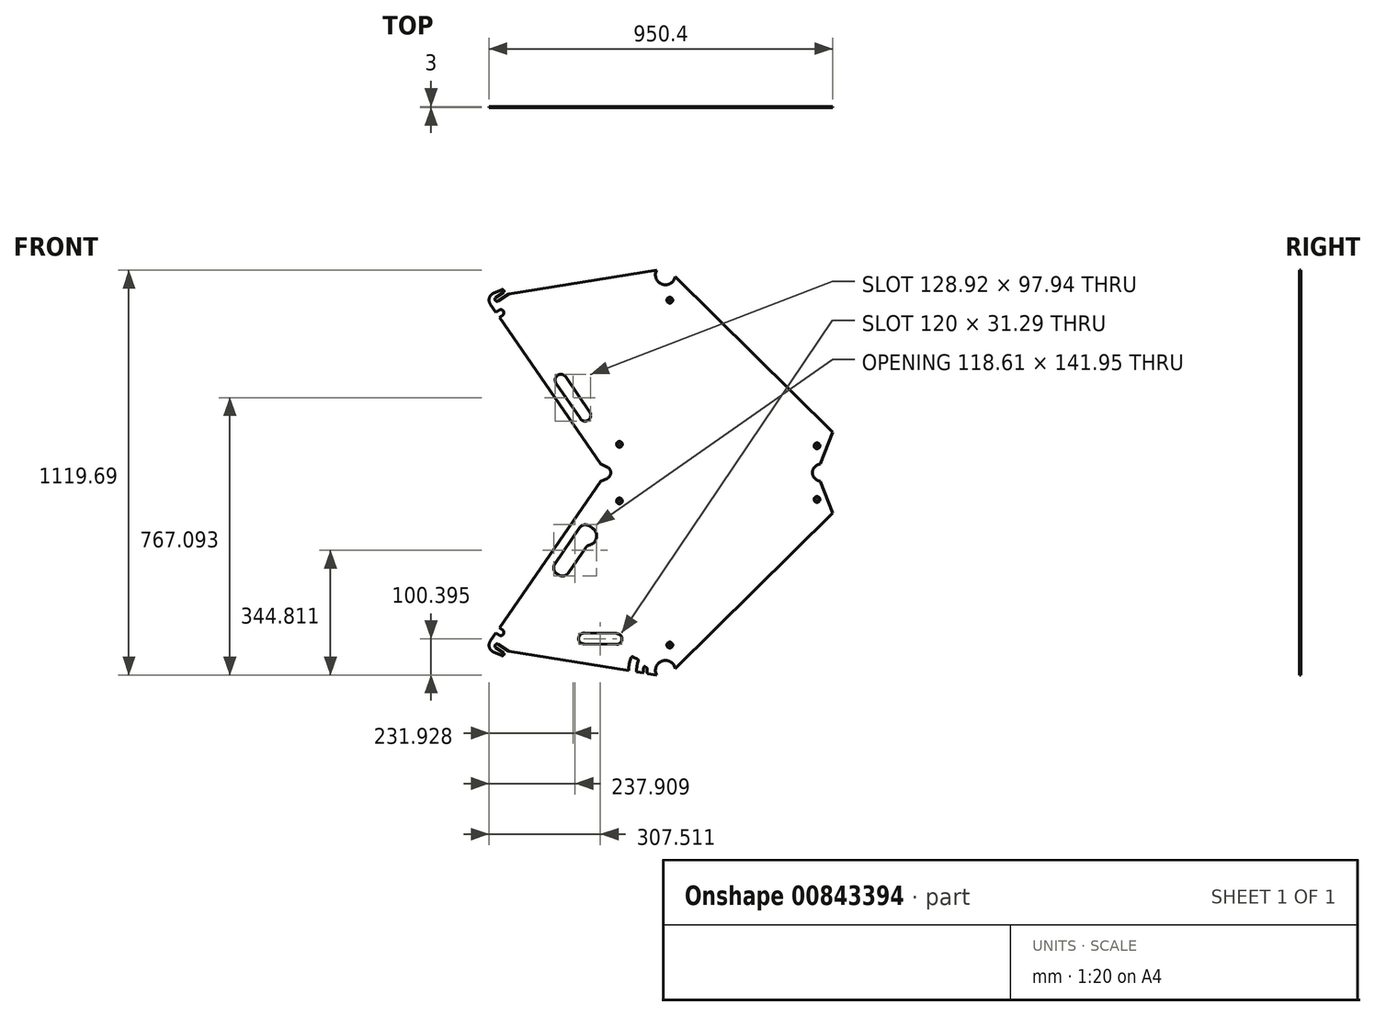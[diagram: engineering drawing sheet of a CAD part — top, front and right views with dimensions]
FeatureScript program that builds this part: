
annotation { "Feature Type Name" : "Feature", "Feature Type Description" : "" }
export const myFeature = defineFeature(function(context is Context, id is Id, definition is map)
    precondition{}
    {
        {
            var Q0;
            Q0=qCreatedBy(makeId("Front.planeOp"),FACE);
            var sketch = newSketch(context, id + "F0", { "sketchPlane" : qUnion([Q0])});
            skCircle(sketch, "E0", {"center": v(1053.9, -134.2) * mm, "radius": 17 * mm, "construction": true});
            skCircle(sketch, "E1", {"center": v(1053.9, -134.2) * mm, "radius": 21.5 * mm, "construction": true});
            skLineSegment(sketch, "E2", {"start": v(622.48, -20.32) * mm, "end": v(871.92, 345.36) * mm, "construction": true});
            skLineSegment(sketch, "E3", {"start": v(615.02, -14.4) * mm, "end": v(879.24, 372.95) * mm, "construction": true});
            skLineSegment(sketch, "E4", {"start": v(1053.9, -134.22) * mm, "end": v(865.03, 414.2) * mm, "construction": true});
            skLineSegment(sketch, "E5", {"start": v(1034.15, -125.7) * mm, "end": v(850, 409.01) * mm, "construction": true});
            skLineSegment(sketch, "E6", {"start": v(861.66, 381.3) * mm, "end": v(851.9, 409.67) * mm, "construction": true});
            skLineSegment(sketch, "E7", {"start": v(1064.21, -115.34) * mm, "end": v(880.07, 419.37) * mm, "construction": true});
            skLineSegment(sketch, "E8", {"start": v(1053.9, -134.2) * mm, "end": v(645.8, -73.78) * mm, "construction": true});
            skLineSegment(sketch, "E9", {"start": v(743.09, -99.4) * mm, "end": v(644.17, -84.76) * mm, "construction": true});
            skLineSegment(sketch, "E10", {"start": v(746.34, -77.44) * mm, "end": v(647.42, -62.8) * mm, "construction": true});
            skLineSegment(sketch, "E11", {"start": v(1035.36, -145.1) * mm, "end": v(841.66, -116.43) * mm, "construction": true});
            skLineSegment(sketch, "E12", {"start": v(1039.32, -118.4) * mm, "end": v(845.61, -89.72) * mm, "construction": true});
            skLineSegment(sketch, "E13", {"start": v(966.15, -134.86) * mm, "end": v(995.58, -139.21) * mm, "construction": true});
            skLineSegment(sketch, "E14", {"start": v(960.23, -139.03) * mm, "end": v(994.85, -144.16) * mm, "construction": true});
            skLineSegment(sketch, "E15", {"start": v(963.6, -143.58) * mm, "end": v(964.04, -140.6) * mm, "construction": true});
            skArc(sketch, "E16", {"start": v(959.64, -143) * mm, "mid": v(959.83, -143.73) * mm, "end": v(960.48, -144.13) * mm, "construction": true});
            skLineSegment(sketch, "E17", {"start": v(960.48, -144.13) * mm, "end": v(962.46, -144.42) * mm, "construction": true});
            skArc(sketch, "E18", {"start": v(962.46, -144.42) * mm, "mid": v(963.2, -144.23) * mm, "end": v(963.6, -143.58) * mm, "construction": true});
            skLineSegment(sketch, "E19", {"start": v(965.3, -133.72) * mm, "end": v(967.21, -120.86) * mm, "construction": true});
            skLineSegment(sketch, "E20", {"start": v(963, -120.24) * mm, "end": v(959.64, -143) * mm, "construction": true});
            skLineSegment(sketch, "E21", {"start": v(962.42, -124.2) * mm, "end": v(966.63, -124.82) * mm, "construction": true});
            skArc(sketch, "E22", {"start": v(965.17, -139.77) * mm, "mid": v(964.43, -139.95) * mm, "end": v(964.04, -140.6) * mm, "construction": true});
            skLineSegment(sketch, "E23", {"start": v(961.7, -129.14) * mm, "end": v(965.9, -129.76) * mm, "construction": true});
            skLineSegment(sketch, "E24", {"start": v(960.08, -126.38) * mm, "end": v(968.24, -127.58) * mm, "construction": true});
            skLineSegment(sketch, "E25", {"start": v(974.82, -141.2) * mm, "end": v(975.55, -136.25) * mm, "construction": true});
            skArc(sketch, "E26", {"start": v(965.3, -133.72) * mm, "mid": v(965.5, -134.46) * mm, "end": v(966.15, -134.86) * mm, "construction": true});
            skLineSegment(sketch, "E27", {"start": v(964.14, -119.4) * mm, "end": v(966.37, -119.73) * mm, "construction": true});
            skArc(sketch, "E28", {"start": v(964.14, -119.4) * mm, "mid": v(963.4, -119.58) * mm, "end": v(963, -120.24) * mm, "construction": true});
            skArc(sketch, "E29", {"start": v(967.21, -120.86) * mm, "mid": v(967.03, -120.12) * mm, "end": v(966.37, -119.73) * mm, "construction": true});
            skLineSegment(sketch, "E30", {"start": v(995.58, -139.21) * mm, "end": v(999.8, -144.9) * mm, "construction": true});
            skLineSegment(sketch, "E31", {"start": v(979.72, -143.94) * mm, "end": v(981.04, -135.04) * mm, "construction": true});
            skArc(sketch, "E32", {"start": v(995.7, -145.3) * mm, "mid": v(995.5, -144.55) * mm, "end": v(994.85, -144.16) * mm, "construction": true});
            skArc(sketch, "E33", {"start": v(995.25, -148.26) * mm, "mid": v(995.44, -149) * mm, "end": v(996.1, -149.4) * mm, "construction": true});
            skArc(sketch, "E34", {"start": v(998.07, -149.7) * mm, "mid": v(998.82, -149.5) * mm, "end": v(999.2, -148.85) * mm, "construction": true});
            skLineSegment(sketch, "E35", {"start": v(996.1, -149.4) * mm, "end": v(998.07, -149.7) * mm, "construction": true});
            skLineSegment(sketch, "E36", {"start": v(999.2, -148.85) * mm, "end": v(999.8, -144.9) * mm, "construction": true});
            skLineSegment(sketch, "E37", {"start": v(995.25, -148.26) * mm, "end": v(995.7, -145.3) * mm, "construction": true});
            skLineSegment(sketch, "E38", {"start": v(985.2, -142.73) * mm, "end": v(985.94, -137.79) * mm, "construction": true});
            skLineSegment(sketch, "E39", {"start": v(995.47, -146.78) * mm, "end": v(993.6, -159.38) * mm, "construction": true});
            skLineSegment(sketch, "E40", {"start": v(850, 409.01) * mm, "end": v(880.07, 419.37) * mm, "construction": true});
            skLineSegment(sketch, "E41", {"start": v(859.77, 380.65) * mm, "end": v(861.66, 381.3) * mm, "construction": true});
            skLineSegment(sketch, "E42", {"start": v(1053.9, -134.22) * mm, "end": v(1520.05, 326.73) * mm, "construction": true});
            skLineSegment(sketch, "E43", {"start": v(1081.03, -129.75) * mm, "end": v(1510.36, 294.78) * mm, "construction": true});
            skLineSegment(sketch, "E44", {"start": v(1060.7, -105.14) * mm, "end": v(1497.91, 327.2) * mm, "construction": true});
            skLineSegment(sketch, "E45", {"start": v(879.24, 372.95) * mm, "end": v(1402.67, 372.95) * mm, "construction": true});
            skLineSegment(sketch, "E46", {"start": v(901.53, 357.05) * mm, "end": v(1486.45, 357.05) * mm, "construction": true});
            skLineSegment(sketch, "E47", {"start": v(890.58, 388.85) * mm, "end": v(1474.25, 388.85) * mm, "construction": true});
            skArc(sketch, "E48", {"start": v(1486.5, 356.93) * mm, "mid": v(1487.54, 375.64) * mm, "end": v(1474.25, 388.85) * mm, "construction": true});
            skArc(sketch, "E49", {"start": v(890.58, 388.85) * mm, "mid": v(888.92, 370.5) * mm, "end": v(901.53, 357.05) * mm, "construction": true});
            skArc(sketch, "E50", {"start": v(1510.36, 294.78) * mm, "mid": v(1511.76, 313.92) * mm, "end": v(1497.91, 327.2) * mm, "construction": true});
            skArc(sketch, "E51", {"start": v(919.09, -223.5) * mm, "mid": v(918.34, -223.31) * mm, "end": v(917.6, -223.13) * mm, "construction": true});
            skFitSpline(sketch, "E52", {"points": [v(871.92, 345.36) * mm, v(875.7, 355.52) * mm, v(881.2, 370.3) * mm, v(868.26, 368.37) * mm, v(864.2, 367.77) * mm], "construction": true});
            skArc(sketch, "E53", {"start": v(591.11, -61.72) * mm, "mid": v(584.1, -63.16) * mm, "end": v(585.54, -70.17) * mm, "construction": true});
            skLineSegment(sketch, "E54", {"start": v(585.54, -70.17) * mm, "end": v(605.08, -83.05) * mm, "construction": true});
            skLineSegment(sketch, "E55", {"start": v(601.55, -93.2) * mm, "end": v(579.26, -83.87) * mm});
            skLineSegment(sketch, "E56", {"start": v(584.15, -63.19) * mm, "end": v(613.37, -82.46) * mm, "construction": true});
            skLineSegment(sketch, "E57", {"start": v(607.46, -8.63) * mm, "end": v(607.4, -8.7) * mm, "construction": true});
            skLineSegment(sketch, "E58", {"start": v(644.18, -84.66) * mm, "end": v(644.29, -83.94) * mm, "construction": true});
            skLineSegment(sketch, "E59", {"start": v(591.11, -61.72) * mm, "end": v(620.67, -81.2) * mm});
            skLineSegment(sketch, "E60", {"start": v(644.18, -84.66) * mm, "end": v(622.66, -81.47) * mm, "construction": true});
            skArc(sketch, "E61", {"start": v(644.63, -83.68) * mm, "mid": v(644.4, -83.74) * mm, "end": v(644.29, -83.94) * mm, "construction": true});
            skLineSegment(sketch, "E62", {"start": v(644.18, -84.66) * mm, "end": v(644.19, -84.63) * mm, "construction": true});
            skArc(sketch, "E63", {"start": v(601.55, -93.2) * mm, "mid": v(607.26, -91.17) * mm, "end": v(605.76, -85.3) * mm});
            skArc(sketch, "E64", {"start": v(617.78, -52.64) * mm, "mid": v(628.06, -58.54) * mm, "end": v(639.47, -61.73) * mm, "construction": true});
            skLineSegment(sketch, "E65", {"start": v(670.48, -77.43) * mm, "end": v(577.33, -63.64) * mm, "construction": true});
            skLineSegment(sketch, "E66", {"start": v(647.4, -62.9) * mm, "end": v(639.47, -61.73) * mm, "construction": true});
            skArc(sketch, "E67", {"start": v(647.3, -63.56) * mm, "mid": v(647.36, -63.78) * mm, "end": v(647.56, -63.9) * mm, "construction": true});
            skLineSegment(sketch, "E68", {"start": v(647.3, -63.56) * mm, "end": v(647.4, -62.9) * mm, "construction": true});
            skArc(sketch, "E69", {"start": v(614, -32.51) * mm, "mid": v(611.92, -43.32) * mm, "end": v(617.78, -52.64) * mm, "construction": true});
            skLineSegment(sketch, "E70", {"start": v(614, -32.51) * mm, "end": v(622.56, -20.17) * mm, "construction": true});
            skLineSegment(sketch, "E71", {"start": v(576.98, -64.11) * mm, "end": v(629.71, 4.8) * mm, "construction": true});
            skArc(sketch, "E72", {"start": v(572.75, -54.03) * mm, "mid": v(569.56, -71.65) * mm, "end": v(582.02, -84.5) * mm, "construction": true});
            skLineSegment(sketch, "E73", {"start": v(607.46, -8.63) * mm, "end": v(608.42, -9.36) * mm, "construction": true});
            skArc(sketch, "E74", {"start": v(621.55, -19.02) * mm, "mid": v(621.5, -19.24) * mm, "end": v(621.6, -19.44) * mm, "construction": true});
            skLineSegment(sketch, "E75", {"start": v(621.6, -19.44) * mm, "end": v(622.56, -20.17) * mm, "construction": true});
            skArc(sketch, "E76", {"start": v(608.42, -9.36) * mm, "mid": v(608.64, -9.42) * mm, "end": v(608.84, -9.3) * mm, "construction": true});
            skLineSegment(sketch, "E77", {"start": v(608.42, -9.36) * mm, "end": v(607.46, -8.63) * mm, "construction": true});
            skLineSegment(sketch, "E78", {"start": v(619.71, -24.29) * mm, "end": v(604.42, -12.6) * mm, "construction": true});
            skCircle(sketch, "E79", {"center": v(600.85, -74.2) * mm, "radius": 5 * mm, "construction": true});
            skLineSegment(sketch, "E80", {"start": v(621.6, -19.44) * mm, "end": v(608.42, -9.36) * mm, "construction": true});
            skLineSegment(sketch, "E81", {"start": v(841.66, -116.43) * mm, "end": v(743.09, -99.4) * mm, "construction": true});
            skLineSegment(sketch, "E82", {"start": v(746.34, -77.44) * mm, "end": v(845.61, -89.72) * mm, "construction": true});
            skEllipse(sketch, "E83", {"center": v(843.64, -103.07) * mm, "majorRadius": 13.5 * mm, "minorRadius": 8.5 * mm, "majorAxis": v(-0.15, -0.99), "construction": true});
            skCircle(sketch, "E84", {"center": v(795.03, 249.5) * mm, "radius": 9.5 * mm, "construction": true});
            skLineSegment(sketch, "E85", {"start": v(796.02, 244.3) * mm, "end": v(795.95, 244.64) * mm, "construction": true});
            skLineSegment(sketch, "E86", {"start": v(796.02, 244.3) * mm, "end": v(789.82, 248.52) * mm, "construction": true});
            skLineSegment(sketch, "E87", {"start": v(784, 242.2) * mm, "end": v(792.26, 236.56) * mm, "construction": true});
            skLineSegment(sketch, "E88", {"start": v(792.26, 236.56) * mm, "end": v(793.8, 238.84) * mm, "construction": true});
            skLineSegment(sketch, "E89", {"start": v(791.91, 236.5) * mm, "end": v(792.26, 236.56) * mm, "construction": true});
            skLineSegment(sketch, "E90", {"start": v(795.95, 244.64) * mm, "end": v(790.17, 248.58) * mm, "construction": true});
            skLineSegment(sketch, "E91", {"start": v(791.91, 236.5) * mm, "end": v(784.06, 241.85) * mm, "construction": true});
            skLineSegment(sketch, "E92", {"start": v(789.96, 238.43) * mm, "end": v(794.75, 245.46) * mm, "construction": true});
            skLineSegment(sketch, "E93", {"start": v(790.2, 238) * mm, "end": v(795.12, 245.2) * mm, "construction": true});
            skLineSegment(sketch, "E94", {"start": v(793.8, 238.84) * mm, "end": v(785.55, 244.47) * mm, "construction": true});
            skLineSegment(sketch, "E95", {"start": v(792.78, 239.54) * mm, "end": v(796.02, 244.3) * mm, "construction": true});
            skArc(sketch, "E96", {"start": v(962.06, -126.67) * mm, "mid": v(930.44, 82.62) * mm, "end": v(787.99, 239.18) * mm, "construction": true});
            skLineSegment(sketch, "E97", {"start": v(702.12, -93.34) * mm, "end": v(670.46, -88.65) * mm, "construction": true});
            skCircle(sketch, "E98", {"center": v(1053.9, -134.2) * mm, "radius": 94.9 * mm, "construction": true});
            skCircle(sketch, "E99", {"center": v(600.85, -74.2) * mm, "radius": 41.4 * mm, "construction": true});
            skLineSegment(sketch, "E100", {"start": v(1055.81, -39.3) * mm, "end": v(601.44, -32.8) * mm, "construction": true});
            skLineSegment(sketch, "E101", {"start": v(1469.36, 401.56) * mm, "end": v(1507.64, 416.26) * mm, "construction": true});
            skLineSegment(sketch, "E102", {"start": v(1507.64, 416.26) * mm, "end": v(1552.44, 299.56) * mm, "construction": true});
            skLineSegment(sketch, "E103", {"start": v(1552.44, 299.56) * mm, "end": v(1514.16, 284.87) * mm, "construction": true});
            skLineSegment(sketch, "E104", {"start": v(1514.16, 284.87) * mm, "end": v(1469.36, 401.56) * mm, "construction": true});
            skLineSegment(sketch, "E105", {"start": v(1516.78, 301.13) * mm, "end": v(1081.03, -129.75) * mm});
            skLineSegment(sketch, "E106", {"start": v(572.75, -54.03) * mm, "end": v(878.77, 388.85) * mm, "construction": true});
            skArc(sketch, "E107", {"start": v(1081.03, -129.75) * mm, "mid": v(1045.11, -108.17) * mm, "end": v(1029.6, -147.1) * mm});
            skLineSegment(sketch, "E108.trimOffspring", {"start": v(1029.6, -147.1) * mm, "end": v(620.67, -81.2) * mm});
            skCircle(sketch, "E109", {"center": v(926.64, 334.5) * mm, "radius": 4 * mm, "construction": true});
            skCircle(sketch, "E110", {"center": v(1472.9, 338.57) * mm, "radius": 4 * mm, "construction": true});
            skCircle(sketch, "E111", {"center": v(1065.9, -64.22) * mm, "radius": 4 * mm, "construction": true});
            skLineSegment(sketch, "E112", {"start": v(1053.9, -134.22) * mm, "end": v(1237.28, -134.22) * mm, "construction": true});
            skLineSegment(sketch, "E113", {"start": v(1053.9, -134.22) * mm, "end": v(1053.9, 23.55) * mm, "construction": true});
            skCircle(sketch, "E114", {"center": v(866.64, 414.5) * mm, "radius": 25 * mm, "construction": true});
            skCircle(sketch, "E115", {"center": v(1489.1, 401.54) * mm, "radius": 28.6 * mm, "construction": true});
            skLineSegment(sketch, "E116", {"start": v(1516.78, 301.13) * mm, "end": v(1482.36, 388.85) * mm});
            skLineSegment(sketch, "E117.trimOffspring", {"start": v(875.12, 388.85) * mm, "end": v(1482.36, 388.85) * mm});
            skCircle(sketch, "E118", {"center": v(600.85, -74.2) * mm, "radius": 312.5 * mm, "construction": true});
            skLineSegment(sketch, "E119.0", {"start": v(570.1, -52.58) * mm, "end": v(585.43, -30.4) * mm});
            skArc(sketch, "E120", {"start": v(570.1, -52.58) * mm, "mid": v(567.23, -70.4) * mm, "end": v(579.26, -83.87) * mm});
            skLineSegment(sketch, "E121.trimOffspring", {"start": v(598.5, -11.47) * mm, "end": v(875.12, 388.85) * mm});
            skArc(sketch, "E122", {"start": v(594.2, -36.46) * mm, "mid": v(610.2, -33.54) * mm, "end": v(607.28, -17.54) * mm, "construction": true});
            skLineSegment(sketch, "E123", {"start": v(600.85, -74.2) * mm, "end": v(600.85, 11.26) * mm, "construction": true});
            skLineSegment(sketch, "E124", {"start": v(594.2, -36.46) * mm, "end": v(585.43, -30.4) * mm, "construction": true});
            skLineSegment(sketch, "E125", {"start": v(607.28, -17.54) * mm, "end": v(598.5, -11.47) * mm, "construction": true});
            skLineSegment(sketch, "E126", {"start": v(598.5, -11.47) * mm, "end": v(595.1, -16.4) * mm});
            skLineSegment(sketch, "E127", {"start": v(595.1, -16.4) * mm, "end": v(603.87, -22.47) * mm});
            skArc(sketch, "E128", {"start": v(594.2, -36.46) * mm, "mid": v(606.03, -34.3) * mm, "end": v(603.87, -22.47) * mm});
            skLineSegment(sketch, "E129", {"start": v(585.43, -30.4) * mm, "end": v(594.2, -36.46) * mm});
            skLineSegment(sketch, "E130", {"start": v(584.23, -71.1) * mm, "end": v(605.76, -85.3) * mm});
            skArc(sketch, "E131", {"start": v(591.11, -61.72) * mm, "mid": v(583.83, -63.6) * mm, "end": v(584.23, -71.1) * mm});
            skSolve(sketch);
        }
        {
            var Q0;
            Q0=qSketchRegion(id+"F0",true);
            extrude(context, id + "F1", {"entities" : qUnion([Q0]), "depth" : 3 * mm, "offsetDistance" : 25 * mm});
        }
        {
            var Q0;
            Q0=makeQuery(id+"F1.opExtrude","SWEPT_FACE",FACE,{"disambiguationData":[OSD([sQuery(id+"F0.wireOp",EDGE,"E117.trimOffspring")])]});
            cPlane(context, id + "F2", {"entities" : qUnion([Q0]), "cplaneType" : CPlaneType.OFFSET, "offset" : 23.9 * mm, "width" : 150 * mm, "height" : 150 * mm});
        }
        {
            var Q0;
            Q0=makeQuery(id+"F1.opExtrude","SWEPT_BODY",BODY,{"disambiguationData":[OSD([sQuery(id+"F0.wireOp",EDGE,"E53"),sQuery(id+"F0.wireOp",EDGE,"E54"),sQuery(id+"F0.wireOp",EDGE,"E55"),sQuery(id+"F0.wireOp",EDGE,"E59"),sQuery(id+"F0.wireOp",EDGE,"c0fece56-cd10-4327-9040-2cab23e675d4"),sQuery(id+"F0.wireOp",EDGE,"E63"),sQuery(id+"F0.wireOp",EDGE,"E72"),sQuery(id+"F0.wireOp",EDGE,"PVY0APLz-6rdr-JrDk-CvCb-vWmYWycaJObT"),sQuery(id+"F0.wireOp",EDGE,"rSiPkJzu-22ck-wLmw-T34Z-YrS7vC3DeLN9"),sQuery(id+"F0.wireOp",EDGE,"E105"),sQuery(id+"F0.wireOp",EDGE,"E106"),sQuery(id+"F0.wireOp",EDGE,"E107"),sQuery(id+"F0.wireOp",EDGE,"E108.trimOffspring")])]});
            var Q1;
            Q1=qCreatedBy(id+"F2.planeOp",FACE);
            mirror(context, id + "F3", {"entities" : qUnion([Q0]), "mirrorPlane" : qUnion([Q1])});
        }
        {
            var Q0;
            Q0=makeQuery(id+"F1.opExtrude","CAP_FACE",FACE,{"disambiguationData":[OSD([sQuery(id+"F0.wireOp",EDGE,"E53"),sQuery(id+"F0.wireOp",EDGE,"E54"),sQuery(id+"F0.wireOp",EDGE,"E55"),sQuery(id+"F0.wireOp",EDGE,"E59"),sQuery(id+"F0.wireOp",EDGE,"c0fece56-cd10-4327-9040-2cab23e675d4"),sQuery(id+"F0.wireOp",EDGE,"E63"),sQuery(id+"F0.wireOp",EDGE,"E72"),sQuery(id+"F0.wireOp",EDGE,"PVY0APLz-6rdr-JrDk-CvCb-vWmYWycaJObT"),sQuery(id+"F0.wireOp",EDGE,"rSiPkJzu-22ck-wLmw-T34Z-YrS7vC3DeLN9"),sQuery(id+"F0.wireOp",EDGE,"E105"),sQuery(id+"F0.wireOp",EDGE,"E106"),sQuery(id+"F0.wireOp",EDGE,"E107"),sQuery(id+"F0.wireOp",EDGE,"E108.trimOffspring")])],"isStart":false});
            var sketch = newSketch(context, id + "F4", { "sketchPlane" : qUnion([Q0])});
            skLineSegment(sketch, "E132", {"start": v(885.12, 412.75) * mm, "end": v(1482.36, 412.75) * mm, "construction": true});
            skLineSegment(sketch, "E133.0", {"start": v(1516.78, 524.37) * mm, "end": v(1482.36, 436.65) * mm, "construction": true});
            skLineSegment(sketch, "E134", {"start": v(1482.36, 388.85) * mm, "end": v(1516.78, 301.13) * mm, "construction": true});
            skArc(sketch, "E135", {"start": v(892.46, 396.86) * mm, "mid": v(902.62, 412.75) * mm, "end": v(892.46, 428.63) * mm});
            skArc(sketch, "E136", {"start": v(1474.77, 433.93) * mm, "mid": v(1459.86, 412.75) * mm, "end": v(1474.77, 391.57) * mm});
            skLineSegment(sketch, "E137", {"start": v(875.12, 388.85) * mm, "end": v(1482.36, 388.85) * mm});
            skLineSegment(sketch, "E138", {"start": v(1482.36, 436.65) * mm, "end": v(875.12, 436.65) * mm});
            skLineSegment(sketch, "E139", {"start": v(875.12, 436.65) * mm, "end": v(892.46, 428.63) * mm});
            skLineSegment(sketch, "E140", {"start": v(875.12, 388.85) * mm, "end": v(892.46, 396.86) * mm});
            skLineSegment(sketch, "E141", {"start": v(1482.36, 388.85) * mm, "end": v(1474.77, 391.57) * mm});
            skLineSegment(sketch, "E142", {"start": v(1482.36, 436.65) * mm, "end": v(1474.77, 433.93) * mm});
            skLineSegment(sketch, "E143", {"start": v(1482.36, 436.65) * mm, "end": v(1482.36, 388.85) * mm, "construction": true});
            skSolve(sketch);
        }
        {
            var Q0;
            Q0=qSketchRegion(id+"F4",true);
            var Q1;
            Q1=makeQuery(id+"F3.opPattern","COPY",FACE,{"derivedFrom":makeQuery(id+"F1.opExtrude","CAP_FACE",FACE,{"disambiguationData":[OSD([sQuery(id+"F0.wireOp",EDGE,"E53"),sQuery(id+"F0.wireOp",EDGE,"E54"),sQuery(id+"F0.wireOp",EDGE,"E55"),sQuery(id+"F0.wireOp",EDGE,"E59"),sQuery(id+"F0.wireOp",EDGE,"c0fece56-cd10-4327-9040-2cab23e675d4"),sQuery(id+"F0.wireOp",EDGE,"E63"),sQuery(id+"F0.wireOp",EDGE,"E72"),sQuery(id+"F0.wireOp",EDGE,"PVY0APLz-6rdr-JrDk-CvCb-vWmYWycaJObT"),sQuery(id+"F0.wireOp",EDGE,"rSiPkJzu-22ck-wLmw-T34Z-YrS7vC3DeLN9"),sQuery(id+"F0.wireOp",EDGE,"E105"),sQuery(id+"F0.wireOp",EDGE,"E106"),sQuery(id+"F0.wireOp",EDGE,"E107"),sQuery(id+"F0.wireOp",EDGE,"E108.trimOffspring")])],"isStart":true}),"instanceName":"1"});
            extrude(context, id + "F5", {"entities" : qUnion([Q0]), "operationType" : NewBodyOperationType.ADD, "endBound" : BoundingType.UP_TO_SURFACE, "oppositeDirection" : true, "depth" : 65 * mm, "endBoundEntityFace" : qUnion([Q1]), "offsetDistance" : 25 * mm});
        }
        {
            var Q0;
            {var subQ0=makeQuery(id+"F1.opExtrude","CAP_FACE",FACE,{"disambiguationData":[OSD([sQuery(id+"F0.wireOp",EDGE,"E53"),sQuery(id+"F0.wireOp",EDGE,"E54"),sQuery(id+"F0.wireOp",EDGE,"E55"),sQuery(id+"F0.wireOp",EDGE,"E59"),sQuery(id+"F0.wireOp",EDGE,"E63"),sQuery(id+"F0.wireOp",EDGE,"E72"),sQuery(id+"F0.wireOp",EDGE,"PVY0APLz-6rdr-JrDk-CvCb-vWmYWycaJObT"),sQuery(id+"F0.wireOp",EDGE,"rSiPkJzu-22ck-wLmw-T34Z-YrS7vC3DeLN9"),sQuery(id+"F0.wireOp",EDGE,"E105"),sQuery(id+"F0.wireOp",EDGE,"E106"),sQuery(id+"F0.wireOp",EDGE,"E107"),sQuery(id+"F0.wireOp",EDGE,"E108.trimOffspring"),sQuery(id+"F0.wireOp",EDGE,"E109"),sQuery(id+"F0.wireOp",EDGE,"E110"),sQuery(id+"F0.wireOp",EDGE,"E111")])],"isStart":false});Q0=makeQuery(id+"F5.boolean.opBoolean","MERGE",FACE,{"derivedFrom":[subQ0,makeQuery(id+"F3.opPattern","COPY",FACE,{"derivedFrom":subQ0,"instanceName":"1"}),makeQuery(id+"F5.opExtrude","CAP_FACE",FACE,{"disambiguationData":[OSD([sQuery(id+"F4.wireOp",EDGE,"yLFeXnhX-FHJ1-lWFD-LUYU-IVhkZNTNpous"),sQuery(id+"F4.wireOp",EDGE,"25Roz2r3-I6Ic-58va-7k2N-V37a2FIcnueW"),sQuery(id+"F4.wireOp",EDGE,"Mdtmx1y3-Aq5y-VBCD-G2xE-9g1DUSUnupkp"),sQuery(id+"F4.wireOp",EDGE,"31XSQ7MP-bYWI-LpWw-hrBR-gacfVsKKRKhD")])],"isStart":true})]});}
            var sketch = newSketch(context, id + "F6", { "sketchPlane" : qUnion([Q0])});
            skLineSegment(sketch, "E144.bottom", {"start": v(829.1, -31.06) * mm, "end": v(919.1, -32.35) * mm});
            skLineSegment(sketch, "E144.top", {"start": v(828.68, -61.06) * mm, "end": v(918.68, -62.35) * mm});
            skArc(sketch, "E145", {"start": v(829.1, -31.06) * mm, "mid": v(813.9, -45.85) * mm, "end": v(828.68, -61.06) * mm});
            skArc(sketch, "E146", {"start": v(918.68, -62.35) * mm, "mid": v(933.89, -47.56) * mm, "end": v(919.1, -32.35) * mm});
            skCircle(sketch, "E147", {"center": v(1053.9, -134.22) * mm, "radius": 101.64 * mm, "construction": true});
            skPoint(sketch, "E148.0", {"position": v(1035.36, -145.1) * mm});
            skLineSegment(sketch, "E149.0", {"start": v(1035.36, -145.1) * mm, "end": v(841.66, -116.43) * mm, "construction": true});
            skPoint(sketch, "E150", {"position": v(952.27, -132.8) * mm});
            skCircle(sketch, "E151", {"center": v(1053.9, -134.22) * mm, "radius": 79.64 * mm, "construction": true});
            skPoint(sketch, "E152", {"position": v(1003.7, -140.42) * mm});
            skCircle(sketch, "E153", {"center": v(1053.9, -134.22) * mm, "radius": 50.57 * mm, "construction": true});
            skCircle(sketch, "E154", {"center": v(1053.9, -134.22) * mm, "radius": 60.57 * mm, "construction": true});
            skArc(sketch, "E155", {"start": v(958.14, -100.13) * mm, "mid": v(953.7, -117.13) * mm, "end": v(952.26, -134.64) * mm});
            skArc(sketch, "E156", {"start": v(978.53, -108.48) * mm, "mid": v(975.03, -123.14) * mm, "end": v(974.36, -138.2) * mm});
            skArc(sketch, "E157", {"start": v(964.95, -97.27) * mm, "mid": v(960.92, -97.2) * mm, "end": v(958.14, -100.13) * mm});
            skLineSegment(sketch, "E158", {"start": v(964.95, -97.27) * mm, "end": v(975.9, -102.33) * mm});
            skArc(sketch, "E159", {"start": v(978.53, -108.48) * mm, "mid": v(978.4, -104.9) * mm, "end": v(975.9, -102.33) * mm});
            skLineSegment(sketch, "E160", {"start": v(952.26, -134.64) * mm, "end": v(974.36, -138.2) * mm});
            skArc(sketch, "E161", {"start": v(993.88, -126.05) * mm, "mid": v(993.33, -133.68) * mm, "end": v(993.74, -141.32) * mm});
            skArc(sketch, "E162", {"start": v(1003.55, -129.43) * mm, "mid": v(1003.37, -136.22) * mm, "end": v(1004.1, -142.99) * mm});
            skLineSegment(sketch, "E163", {"start": v(998.61, -124.02) * mm, "end": v(1002.33, -126.71) * mm});
            skPoint(sketch, "E164.visualSharp", {"position": v(994.74, -121.22) * mm});
            skArc(sketch, "E164.filletArc", {"start": v(998.61, -124.02) * mm, "mid": v(995.67, -123.7) * mm, "end": v(993.88, -126.05) * mm});
            skPoint(sketch, "E165.visualSharp", {"position": v(1003.74, -127.74) * mm});
            skArc(sketch, "E165.filletArc", {"start": v(1003.55, -129.43) * mm, "mid": v(1003.3, -127.9) * mm, "end": v(1002.33, -126.71) * mm});
            skLineSegment(sketch, "E166", {"start": v(993.74, -141.32) * mm, "end": v(1004.1, -142.99) * mm});
            skSolve(sketch);
        }
        {
            var Q0;
            Q0=qSketchRegion(id+"F6",true);
            extrude(context, id + "F7", {"entities" : qUnion([Q0]), "operationType" : NewBodyOperationType.REMOVE, "oppositeDirection" : true, "depth" : 25 * mm, "offsetDistance" : 25 * mm});
        }
        {
            var Q0;
            Q0=makeQuery(id+"F4.imprint","IMPRINT",FACE,{"disambiguationData":[TD([[makeQuery(id+"F4.imprint","IMPRINT",EDGE,{"derivedFrom":sQuery(id+"F4.wireOp",EDGE,"E137")}),-1.0]])]});
            var sketch = newSketch(context, id + "F8", { "sketchPlane" : qUnion([Q0])});
            skLineSegment(sketch, "E167", {"start": v(748.46, 160.82) * mm, "end": v(816.08, 259.96) * mm});
            skLineSegment(sketch, "E168", {"start": v(843.88, 265.2) * mm, "end": v(852.14, 259.57) * mm});
            skLineSegment(sketch, "E169", {"start": v(757.84, 130.21) * mm, "end": v(753.71, 133.03) * mm});
            skCircle(sketch, "E170.0", {"center": v(600.85, -74.2) * mm, "radius": 312.5 * mm, "construction": true});
            skLineSegment(sketch, "E170.1", {"start": v(622.48, -20.32) * mm, "end": v(871.92, 345.36) * mm, "construction": true});
            skLineSegment(sketch, "E171.0", {"start": v(885.12, 412.75) * mm, "end": v(1482.36, 412.75) * mm, "construction": true});
            skCircle(sketch, "E172.MirrorC", {"center": v(600.85, 899.7) * mm, "radius": 312.5 * mm, "construction": true});
            skLineSegment(sketch, "E173.MirrorCS", {"start": v(622.48, 845.82) * mm, "end": v(871.92, 480.13) * mm, "construction": true});
            skLineSegment(sketch, "E174", {"start": v(818.34, 562.24) * mm, "end": v(751.84, 659.72) * mm});
            skLineSegment(sketch, "E175", {"start": v(756.04, 681.95) * mm, "end": v(756.04, 681.95) * mm});
            skLineSegment(sketch, "E176", {"start": v(778.28, 677.75) * mm, "end": v(844.77, 580.27) * mm});
            skLineSegment(sketch, "E177", {"start": v(840.57, 558.04) * mm, "end": v(840.57, 558.04) * mm});
            skLineSegment(sketch, "E178.0", {"start": v(797.53, 236.3) * mm, "end": v(785.55, 244.47) * mm, "construction": true});
            skLineSegment(sketch, "E179.MirrorCS", {"start": v(797.53, 589.2) * mm, "end": v(785.55, 581.03) * mm, "construction": true});
            skLineSegment(sketch, "E180", {"start": v(797.53, 589.2) * mm, "end": v(768.19, 569.19) * mm, "construction": true});
            skPoint(sketch, "E181.orphan", {"position": v(793.8, 586.66) * mm});
            skPoint(sketch, "E182.orphan", {"position": v(793.8, 238.84) * mm});
            skLineSegment(sketch, "E183", {"start": v(797.53, 236.3) * mm, "end": v(778.55, 249.24) * mm, "construction": true});
            skPoint(sketch, "E184.visualSharp", {"position": v(827.35, 276.48) * mm});
            skArc(sketch, "E184.filletArc", {"start": v(843.88, 265.2) * mm, "mid": v(828.9, 268.34) * mm, "end": v(816.08, 259.96) * mm});
            skPoint(sketch, "E185.visualSharp", {"position": v(872.79, 245.49) * mm});
            skArc(sketch, "E185.filletArc", {"start": v(842.48, 211.69) * mm, "mid": v(863.19, 232.43) * mm, "end": v(852.14, 259.57) * mm});
            skPoint(sketch, "E186.visualSharp", {"position": v(737.2, 144.3) * mm});
            skArc(sketch, "E186.filletArc", {"start": v(748.46, 160.82) * mm, "mid": v(745.33, 145.84) * mm, "end": v(753.71, 133.03) * mm});
            skPoint(sketch, "E187.visualSharp", {"position": v(782.63, 113.3) * mm});
            skArc(sketch, "E187.filletArc", {"start": v(757.84, 130.21) * mm, "mid": v(772.83, 127.08) * mm, "end": v(785.64, 135.47) * mm});
            skPoint(sketch, "E188.visualSharp", {"position": v(742.83, 672.94) * mm});
            skArc(sketch, "E188.filletArc", {"start": v(756.04, 681.95) * mm, "mid": v(749.34, 671.7) * mm, "end": v(751.84, 659.72) * mm});
            skPoint(sketch, "E189.visualSharp", {"position": v(769.26, 690.97) * mm});
            skArc(sketch, "E189.filletArc", {"start": v(778.28, 677.75) * mm, "mid": v(768.03, 684.46) * mm, "end": v(756.04, 681.95) * mm});
            skPoint(sketch, "E190.visualSharp", {"position": v(853.79, 567.05) * mm});
            skArc(sketch, "E190.filletArc", {"start": v(840.57, 558.04) * mm, "mid": v(847.28, 568.28) * mm, "end": v(844.77, 580.27) * mm});
            skPoint(sketch, "E191.visualSharp", {"position": v(827.35, 549.02) * mm});
            skArc(sketch, "E191.filletArc", {"start": v(818.34, 562.24) * mm, "mid": v(828.58, 555.53) * mm, "end": v(840.57, 558.04) * mm});
            skLineSegment(sketch, "E192", {"start": v(785.64, 135.47) * mm, "end": v(833.6, 205.8) * mm});
            skArc(sketch, "E193", {"start": v(842.48, 211.69) * mm, "mid": v(837.47, 209.6) * mm, "end": v(833.6, 205.8) * mm});
            skSolve(sketch);
        }
        {
            var Q0;
            Q0=qSketchRegion(id+"F8",true);
            extrude(context, id + "F9", {"entities" : qUnion([Q0]), "operationType" : NewBodyOperationType.REMOVE, "endBound" : BoundingType.THROUGH_ALL, "oppositeDirection" : true, "depth" : 25 * mm, "offsetDistance" : 25 * mm});
        }
        {
            var Q0;
            Q0=makeQuery(id+"F4.imprint","IMPRINT",FACE,{"disambiguationData":[TD([[makeQuery(id+"F4.imprint","IMPRINT",EDGE,{"derivedFrom":sQuery(id+"F4.wireOp",EDGE,"E137")}),-1.0]])]});
            var sketch = newSketch(context, id + "F10", { "sketchPlane" : qUnion([Q0])});
            skPoint(sketch, "E194.0", {"position": v(926.64, 334.5) * mm});
            skPoint(sketch, "E194.1", {"position": v(1472.9, 338.57) * mm});
            skPoint(sketch, "E194.2", {"position": v(1065.9, -64.22) * mm});
            skPoint(sketch, "E195.MirrorP", {"position": v(926.64, 491) * mm});
            skPoint(sketch, "E196.MirrorP", {"position": v(1472.9, 486.93) * mm});
            skPoint(sketch, "E197.MirrorP", {"position": v(1065.9, 889.72) * mm});
            skSolve(sketch);
        }
        {
            var Q0;
            Q0=sQuery(id+"F10.wireOp",VERTEX,"E197.MirrorP");
            var Q1;
            Q1=sQuery(id+"F10.wireOp",VERTEX,"E195.MirrorP");
            var Q2;
            Q2=sQuery(id+"F10.wireOp",VERTEX,"E196.MirrorP");
            var Q3;
            Q3=sQuery(id+"F0.wireOp",VERTEX,"E109.center");
            var Q4;
            Q4=sQuery(id+"F0.wireOp",VERTEX,"E110.center");
            var Q5;
            Q5=sQuery(id+"F0.wireOp",VERTEX,"E111.center");
            var Q6;
            Q6=sQuery(id+"F10.wireOp",VERTEX,"E194.2");
            var Q7;
            Q7=sQuery(id+"F10.wireOp",VERTEX,"E194.0");
            var Q8;
            Q8=sQuery(id+"F10.wireOp",VERTEX,"E194.1");
            var Q9;
            Q9=makeQuery(id+"F1.opExtrude","SWEPT_BODY",BODY,{"disambiguationData":[OSD([sQuery(id+"F0.wireOp",EDGE,"E53"),sQuery(id+"F0.wireOp",EDGE,"E54"),sQuery(id+"F0.wireOp",EDGE,"E55"),sQuery(id+"F0.wireOp",EDGE,"E59"),sQuery(id+"F0.wireOp",EDGE,"E63"),sQuery(id+"F0.wireOp",EDGE,"E105"),sQuery(id+"F0.wireOp",EDGE,"E107"),sQuery(id+"F0.wireOp",EDGE,"E108.trimOffspring"),sQuery(id+"F0.wireOp",EDGE,"E116"),sQuery(id+"F0.wireOp",EDGE,"E117.trimOffspring"),sQuery(id+"F0.wireOp",EDGE,"E119.0"),sQuery(id+"F0.wireOp",EDGE,"E120"),sQuery(id+"F0.wireOp",EDGE,"E121.trimOffspring"),sQuery(id+"F0.wireOp",EDGE,"E122"),sQuery(id+"F0.wireOp",EDGE,"E124"),sQuery(id+"F0.wireOp",EDGE,"E125")])]});
            hole(context, id + "F11", {"style" : HoleStyle.C_SINK, "endStyle" : HoleEndStyle.THROUGH, "holeDiameter" : 8 * mm, "cSinkDiameter" : 16 * mm, "cSinkAngle" : 90 * degree, "majorDiameter" : 5 * mm, "isTappedThrough" : true, "tappedDepth" : 12 * mm, "tapClearance" : 3, "locations" : qUnion([Q0, Q1, Q2, Q3, Q4, Q5, Q6, Q7, Q8]), "scope" : qUnion([Q9])});
        }
    });
